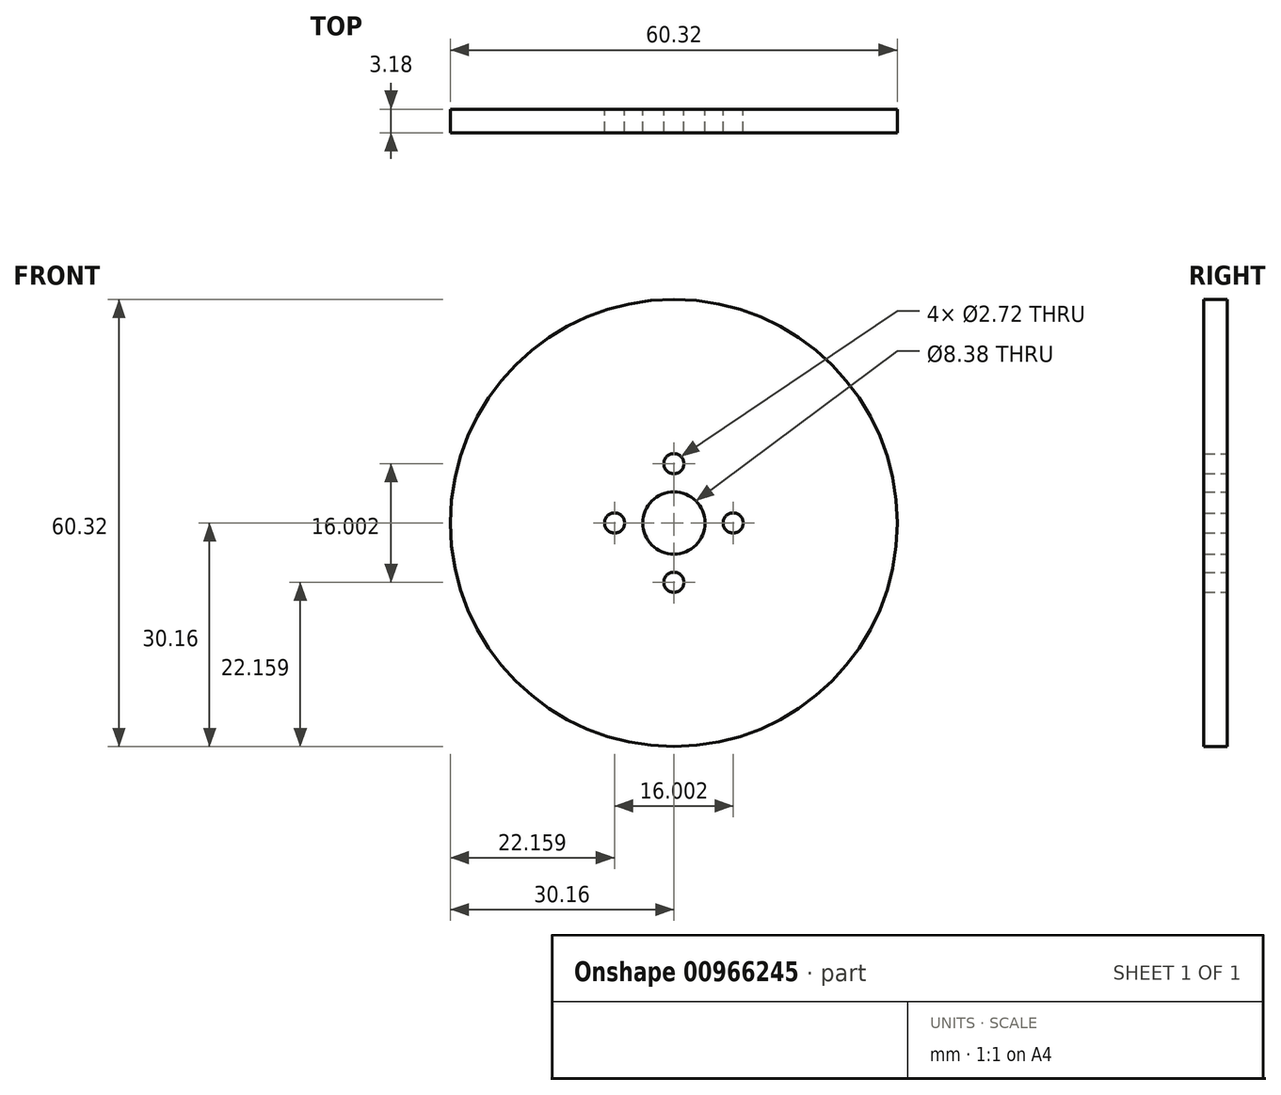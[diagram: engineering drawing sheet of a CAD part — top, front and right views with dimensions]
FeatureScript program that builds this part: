
annotation { "Feature Type Name" : "Feature", "Feature Type Description" : "" }
export const myFeature = defineFeature(function(context is Context, id is Id, definition is map)
    precondition{}
    {
        {
            var Q0;
            Q0=qCreatedBy(makeId("Front.planeOp"),FACE);
            var sketch = newSketch(context, id + "F0", { "sketchPlane" : qUnion([Q0])});
            skCircle(sketch, "E0", {"center": v(0, 0) * mm, "radius": 30.16 * mm});
            skCircle(sketch, "E1", {"center": v(0, 0) * mm, "radius": 4.2 * mm});
            skCircle(sketch, "E2", {"center": v(0, 8) * mm, "radius": 1.36 * mm});
            skCircle(sketch, "E3.1.0", {"center": v(-8, 0) * mm, "radius": 1.36 * mm});
            skCircle(sketch, "E3.2.0", {"center": v(0, -8) * mm, "radius": 1.36 * mm});
            skCircle(sketch, "E3.3.0", {"center": v(8, 0) * mm, "radius": 1.36 * mm});
            skSolve(sketch);
        }
        {
            var Q0;
            Q0=makeQuery(id+"F0.imprint","IMPRINT",FACE,{"disambiguationData":[TD([[makeQuery(id+"F0.imprint","IMPRINT",EDGE,{"derivedFrom":sQuery(id+"F0.wireOp",EDGE,"E0")}),1.0]])]});
            extrude(context, id + "F1", {"entities" : qUnion([Q0]), "depth" : 3.17 * mm});
        }
    });
